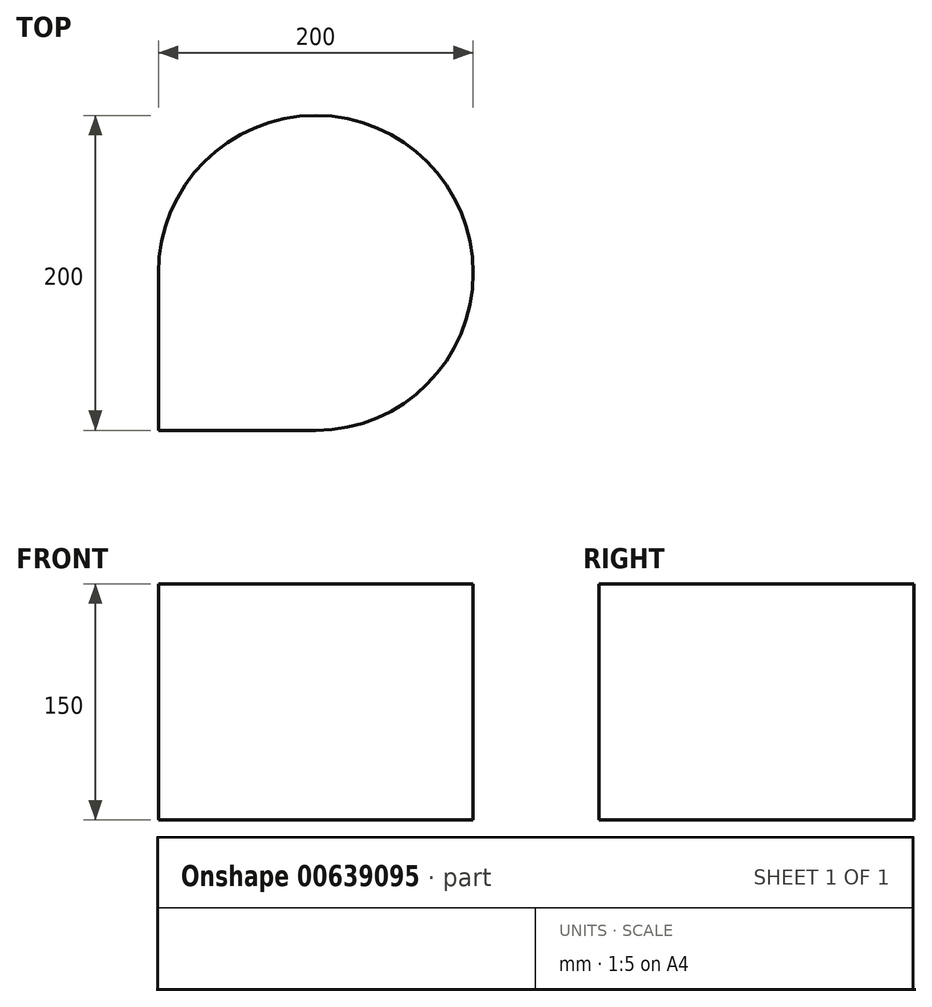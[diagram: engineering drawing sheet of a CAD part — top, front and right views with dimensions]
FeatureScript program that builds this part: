
annotation { "Feature Type Name" : "Feature", "Feature Type Description" : "" }
export const myFeature = defineFeature(function(context is Context, id is Id, definition is map)
    precondition{}
    {
        {
            var Q0;
            Q0=qCreatedBy(makeId("Top.planeOp"),FACE);
            var sketch = newSketch(context, id + "F0", { "sketchPlane" : qUnion([Q0])});
            skLineSegment(sketch, "E0", {"start": v(-100, 0) * mm, "end": v(-100, -100) * mm});
            skLineSegment(sketch, "E1", {"start": v(-100, -100) * mm, "end": v(0, -100) * mm});
            skArc(sketch, "E2", {"start": v(-100, 0) * mm, "mid": v(70.71, 70.71) * mm, "end": v(0, -100) * mm});
            skSolve(sketch);
        }
        {
            var Q0;
            Q0=makeQuery(id+"F0.imprint","IMPRINT",FACE,{"disambiguationData":[TD([[makeQuery(id+"F0.imprint","IMPRINT",EDGE,{"derivedFrom":sQuery(id+"F0.wireOp",EDGE,"E0")}),1.0]])]});
            extrude(context, id + "F1", {"entities" : qUnion([Q0]), "depth" : 150 * mm, "offsetDistance" : 25 * mm});
        }
    });
